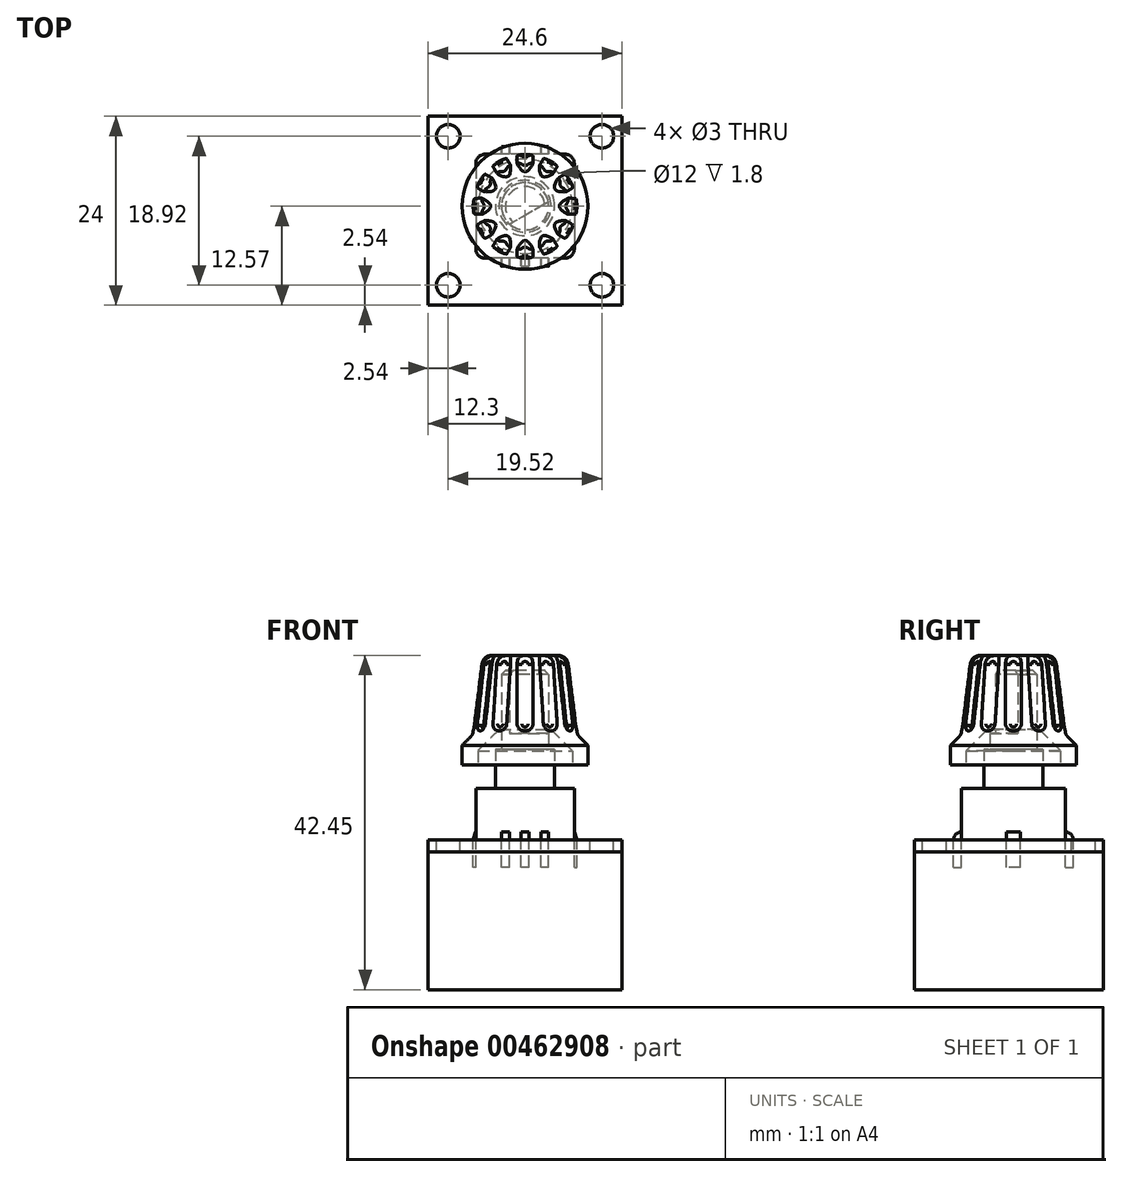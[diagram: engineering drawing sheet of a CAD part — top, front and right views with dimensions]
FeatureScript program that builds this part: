
annotation { "Feature Type Name" : "Feature", "Feature Type Description" : "" }
export const myFeature = defineFeature(function(context is Context, id is Id, definition is map)
    precondition{}
    {
        {
            var Q0;
            Q0=qCreatedBy(makeId("Top.planeOp"),FACE);
            var sketch = newSketch(context, id + "F0", { "sketchPlane" : qUnion([Q0])});
            skLineSegment(sketch, "E0.bottom", {"start": v(6.25, 6.6) * mm, "end": v(-6.25, 6.6) * mm});
            skLineSegment(sketch, "E0.top", {"start": v(6.25, -6.6) * mm, "end": v(-6.25, -6.6) * mm});
            skLineSegment(sketch, "E0.left", {"start": v(6.25, 6.6) * mm, "end": v(6.25, -6.6) * mm});
            skLineSegment(sketch, "E0.right", {"start": v(-6.25, 6.6) * mm, "end": v(-6.25, -6.6) * mm});
            skPoint(sketch, "E0.middle", {"position": v(0, 0) * mm});
            skArc(sketch, "E1", {"start": v(6.25, 5.46) * mm, "mid": v(5.92, 6.27) * mm, "end": v(5.1, 6.6) * mm});
            skArc(sketch, "E2", {"start": v(-6.25, 5.46) * mm, "mid": v(-5.92, 6.27) * mm, "end": v(-5.1, 6.6) * mm});
            skLineSegment(sketch, "E3", {"start": v(0, 0) * mm, "end": v(0, 0) * mm});
            skPoint(sketch, "E3.endSnap0", {"position": v(6.25, 0) * mm});
            skLineSegment(sketch, "E4", {"start": v(0, 0) * mm, "end": v(0, 9.01) * mm, "construction": true});
            skArc(sketch, "E5.MirrorCS", {"start": v(-6.25, -5.46) * mm, "mid": v(-5.92, -6.27) * mm, "end": v(-5.1, -6.6) * mm});
            skArc(sketch, "E6.MirrorCS", {"start": v(6.25, -5.46) * mm, "mid": v(5.92, -6.27) * mm, "end": v(5.1, -6.6) * mm});
            skCircle(sketch, "E7", {"center": v(0, 0) * mm, "radius": 3.75 * mm});
            skCircle(sketch, "E8", {"center": v(0, 0) * mm, "radius": 3 * mm});
            skLineSegment(sketch, "E9", {"start": v(6.25, 0.9) * mm, "end": v(6.6, 0.9) * mm});
            skLineSegment(sketch, "E10", {"start": v(6.6, 0.9) * mm, "end": v(6.6, -0.9) * mm});
            skLineSegment(sketch, "E11", {"start": v(6.6, -0.9) * mm, "end": v(6.25, -0.9) * mm});
            skLineSegment(sketch, "E12", {"start": v(-6.25, 0.9) * mm, "end": v(-6.6, 0.9) * mm});
            skLineSegment(sketch, "E13", {"start": v(-6.6, 0.9) * mm, "end": v(-6.6, -0.9) * mm});
            skLineSegment(sketch, "E14", {"start": v(-6.6, -0.9) * mm, "end": v(-6.25, -0.9) * mm});
            skPoint(sketch, "E15", {"position": v(6.6, 0) * mm});
            skLineSegment(sketch, "E16", {"start": v(-0.5, -6.6) * mm, "end": v(-0.5, -7.6) * mm});
            skLineSegment(sketch, "E17", {"start": v(-0.5, -7.6) * mm, "end": v(0.5, -7.6) * mm});
            skLineSegment(sketch, "E18", {"start": v(0.5, -7.6) * mm, "end": v(0.5, -6.6) * mm});
            skPoint(sketch, "E19", {"position": v(0, -7.6) * mm});
            skLineSegment(sketch, "E20", {"start": v(2, -6.6) * mm, "end": v(2, -7.6) * mm});
            skLineSegment(sketch, "E21", {"start": v(2, -7.6) * mm, "end": v(3, -7.6) * mm});
            skLineSegment(sketch, "E22", {"start": v(3, -7.6) * mm, "end": v(3, -6.6) * mm});
            skLineSegment(sketch, "E23", {"start": v(-2, -6.6) * mm, "end": v(-2, -7.6) * mm});
            skLineSegment(sketch, "E24", {"start": v(-2, -7.6) * mm, "end": v(-3, -7.6) * mm});
            skLineSegment(sketch, "E25", {"start": v(-3, -7.6) * mm, "end": v(-3, -6.6) * mm});
            skPoint(sketch, "E26", {"position": v(-2.5, -7.6) * mm});
            skPoint(sketch, "E27", {"position": v(2.5, -7.6) * mm});
            skLineSegment(sketch, "E28", {"start": v(-2, -7.6) * mm, "end": v(-0.5, -7.6) * mm, "construction": true});
            skLineSegment(sketch, "E29", {"start": v(0.5, -7.6) * mm, "end": v(2, -7.6) * mm, "construction": true});
            skLineSegment(sketch, "E30.MirrorCS", {"start": v(-3, 7.6) * mm, "end": v(-3, 6.6) * mm});
            skLineSegment(sketch, "E31.MirrorCS", {"start": v(-2, 7.6) * mm, "end": v(-3, 7.6) * mm});
            skLineSegment(sketch, "E32.MirrorCS", {"start": v(-2, 6.6) * mm, "end": v(-2, 7.6) * mm});
            skLineSegment(sketch, "E33.MirrorCS", {"start": v(2, 6.6) * mm, "end": v(2, 7.6) * mm});
            skLineSegment(sketch, "E34.MirrorCS", {"start": v(2, 7.6) * mm, "end": v(3, 7.6) * mm});
            skLineSegment(sketch, "E35.MirrorCS", {"start": v(3, 7.6) * mm, "end": v(3, 6.6) * mm});
            skLineSegment(sketch, "E36", {"start": v(2.95, 0.55) * mm, "end": v(-1.95, -2.28) * mm});
            skLineSegment(sketch, "E37", {"start": v(0, 0) * mm, "end": v(10.13, 0) * mm, "construction": true});
            skLineSegment(sketch, "E38", {"start": v(0, 0) * mm, "end": v(-2.6, -1.5) * mm, "construction": true});
            skSolve(sketch);
        }
        {
            var Q0;
            {var subQ3=sQuery(id+"F0.wireOp",EDGE,"CTmPjIdn-6teS-sF9U-aKKL-pw7HEeKchRhR");Q0=makeQuery(id+"F0.imprint","IMPRINT",FACE,{"disambiguationData":[TD([[makeQuery(id+"F0.imprint","IMPRINT",EDGE,{"derivedFrom":subQ3}),1.0]])]});}
            var Q1;
            Q1=makeQuery(id+"F0.imprint","IMPRINT",FACE,{"disambiguationData":[TD([[makeQuery(id+"F0.imprint","IMPRINT",EDGE,{"derivedFrom":sQuery(id+"F0.wireOp",EDGE,"E7")}),1.0]])]});
            var Q2;
            Q2=makeQuery(id+"F0.imprint","IMPRINT",FACE,{"disambiguationData":[TD([[makeQuery(id+"F0.imprint","IMPRINT",EDGE,{"derivedFrom":sQuery(id+"F0.wireOp",EDGE,"E8")}),1.0]])]});
            var Q3;
            {var subQ3=sQuery(id+"F0.wireOp",EDGE,"E1");Q3=makeQuery(id+"F0.imprint","IMPRINT",FACE,{"disambiguationData":[TD([[makeQuery(id+"F0.imprint","IMPRINT",EDGE,{"derivedFrom":subQ3}),1.0]])]});}
            extrude(context, id + "F1", {"entities" : qUnion([Q0, Q1, Q2, Q3]), "oppositeDirection" : true, "depth" : 6.5 * mm, "offsetDistance" : 25.4 * mm});
        }
        {
            var Q0;
            Q0=makeQuery(id+"F0.imprint","IMPRINT",FACE,{"disambiguationData":[TD([[makeQuery(id+"F0.imprint","IMPRINT",EDGE,{"derivedFrom":sQuery(id+"F0.wireOp",EDGE,"E7")}),1.0]])]});
            extrude(context, id + "F2", {"entities" : qUnion([Q0]), "operationType" : NewBodyOperationType.ADD, "depth" : 5 * mm, "offsetDistance" : 25.4 * mm});
        }
        {
            var Q0;
            {var subQ0=sQuery(id+"F0.wireOp",EDGE,"E36");Q0=makeQuery(id+"F0.imprint","IMPRINT",FACE,{"disambiguationData":[TD([[makeQuery(id+"F0.imprint","IMPRINT",EDGE,{"derivedFrom":subQ0}),-1.0]])]});}
            extrude(context, id + "F3", {"entities" : qUnion([Q0]), "depth" : 15 * mm, "offsetDistance" : 25.4 * mm});
        }
        {
            var Q0;
            {var subQ0=sQuery(id+"F0.wireOp",EDGE,"E36");Q0=makeQuery(id+"F0.imprint","IMPRINT",FACE,{"disambiguationData":[TD([[makeQuery(id+"F0.imprint","IMPRINT",EDGE,{"derivedFrom":subQ0}),1.0]])]});}
            extrude(context, id + "F4", {"entities" : qUnion([Q0]), "operationType" : NewBodyOperationType.ADD, "depth" : 13 * mm - 6 * mm, "offsetDistance" : 25.4 * mm});
        }
        {
            var Q0;
            Q0=makeQuery(id+"F3.opExtrude","CAP_EDGE",EDGE,{"disambiguationData":[OSD([sQuery(id+"F0.wireOp",EDGE,"E8")])],"isStart":false});
            chamfer(context, id + "F5", {"entities" : qUnion([Q0]), "width" : .5 * mm, "tangentPropagation" : true});
        }
        {
            var Q0;
            {var subQ0=sQuery(id+"F0.wireOp",EDGE,"E12");Q0=makeQuery(id+"F0.imprint","IMPRINT",FACE,{"disambiguationData":[TD([[makeQuery(id+"F0.imprint","IMPRINT",EDGE,{"derivedFrom":subQ0}),1.0]])]});}
            var Q1;
            {var subQ0=sQuery(id+"F0.wireOp",EDGE,"E9");Q1=makeQuery(id+"F0.imprint","IMPRINT",FACE,{"disambiguationData":[TD([[makeQuery(id+"F0.imprint","IMPRINT",EDGE,{"derivedFrom":subQ0}),-1.0]])]});}
            extrude(context, id + "F6", {"entities" : qUnion([Q0, Q1]), "operationType" : NewBodyOperationType.ADD, "oppositeDirection" : true, "depth" : 10 * mm, "offsetDistance" : 25.4 * mm, "hasSecondDirection" : true, "secondDirectionOppositeDirection" : true, "secondDirectionDepth" : 5.5 * mm});
        }
        {
            var Q0;
            {var subQ0=sQuery(id+"F0.wireOp",EDGE,"E23");Q0=makeQuery(id+"F0.imprint","IMPRINT",FACE,{"disambiguationData":[TD([[makeQuery(id+"F0.imprint","IMPRINT",EDGE,{"derivedFrom":subQ0}),-1.0]])]});}
            var Q1;
            {var subQ0=sQuery(id+"F0.wireOp",EDGE,"E16");Q1=makeQuery(id+"F0.imprint","IMPRINT",FACE,{"disambiguationData":[TD([[makeQuery(id+"F0.imprint","IMPRINT",EDGE,{"derivedFrom":subQ0}),1.0]])]});}
            var Q2;
            {var subQ0=sQuery(id+"F0.wireOp",EDGE,"E20");Q2=makeQuery(id+"F0.imprint","IMPRINT",FACE,{"disambiguationData":[TD([[makeQuery(id+"F0.imprint","IMPRINT",EDGE,{"derivedFrom":subQ0}),1.0]])]});}
            var Q3;
            {var subQ0=sQuery(id+"F0.wireOp",EDGE,"E30.MirrorCS");Q3=makeQuery(id+"F0.imprint","IMPRINT",FACE,{"disambiguationData":[TD([[makeQuery(id+"F0.imprint","IMPRINT",EDGE,{"derivedFrom":subQ0}),1.0]])]});}
            var Q4;
            {var subQ0=sQuery(id+"F0.wireOp",EDGE,"E33.MirrorCS");Q4=makeQuery(id+"F0.imprint","IMPRINT",FACE,{"disambiguationData":[TD([[makeQuery(id+"F0.imprint","IMPRINT",EDGE,{"derivedFrom":subQ0}),-1.0]])]});}
            extrude(context, id + "F7", {"entities" : qUnion([Q0, Q1, Q2, Q3, Q4]), "operationType" : NewBodyOperationType.ADD, "oppositeDirection" : true, "depth" : 10 * mm, "offsetDistance" : 25.4 * mm, "hasSecondDirection" : true, "secondDirectionOppositeDirection" : true, "secondDirectionDepth" : 5.5 * mm});
        }
        {
            var Q0;
            Q0=makeQuery(id+"F7.opExtrude","CAP_EDGE",EDGE,{"disambiguationData":[OSD([sQuery(id+"F0.wireOp",EDGE,"E24")])],"isStart":true});
            var Q1;
            Q1=makeQuery(id+"F7.opExtrude","CAP_EDGE",EDGE,{"disambiguationData":[OSD([sQuery(id+"F0.wireOp",EDGE,"E17")])],"isStart":true});
            var Q2;
            Q2=makeQuery(id+"F7.opExtrude","CAP_EDGE",EDGE,{"disambiguationData":[OSD([sQuery(id+"F0.wireOp",EDGE,"E21")])],"isStart":true});
            var Q3;
            Q3=makeQuery(id+"F7.opExtrude","CAP_EDGE",EDGE,{"disambiguationData":[OSD([sQuery(id+"F0.wireOp",EDGE,"E34.MirrorCS")])],"isStart":true});
            var Q4;
            Q4=makeQuery(id+"F7.opExtrude","CAP_EDGE",EDGE,{"disambiguationData":[OSD([sQuery(id+"F0.wireOp",EDGE,"E31.MirrorCS")])],"isStart":true});
            fillet(context, id + "F8", {"entities" : qUnion([Q0, Q1, Q2, Q3, Q4]), "radius" : 1 * mm, "tangentPropagation" : true, "allowEdgeOverflow" : false});
        }
        {
            var Q0;
            Q0=makeQuery(id+"F6.opExtrude","CAP_EDGE",EDGE,{"disambiguationData":[OSD([sQuery(id+"F0.wireOp",EDGE,"E10")])],"isStart":true});
            chamfer(context, id + "F9", {"entities" : qUnion([Q0]), "chamferType" : ChamferType.TWO_OFFSETS, "width1" : 1 * mm, "oppositeDirection" : false, "width2" : .3 * mm, "tangentPropagation" : true});
        }
        {
            var Q0;
            Q0=makeQuery(id+"F6.opExtrude","CAP_EDGE",EDGE,{"disambiguationData":[OSD([sQuery(id+"F0.wireOp",EDGE,"E13")])],"isStart":true});
            chamfer(context, id + "F10", {"entities" : qUnion([Q0]), "chamferType" : ChamferType.TWO_OFFSETS, "width1" : .3 * mm, "oppositeDirection" : false, "width2" : 1 * mm, "tangentPropagation" : true});
        }
        {
            var Q0;
            Q0=qCreatedBy(makeId("Top.planeOp"),FACE);
            cPlane(context, id + "F11", {"entities" : qUnion([Q0]), "cplaneType" : CPlaneType.OFFSET, "offset" : 3 * mm, "width" : 152.4 * mm, "height" : 152.4 * mm});
        }
        {
            var Q0;
            Q0=qCreatedBy(id+"F11.planeOp",FACE);
            var sketch = newSketch(context, id + "F12", { "sketchPlane" : qUnion([Q0])});
            skLineSegment(sketch, "E39", {"start": v(-9.63, 0) * mm, "end": v(11.95, 0) * mm, "construction": true});
            skSolve(sketch);
        }
        {
            var Q0;
            Q0=qCreatedBy(makeId("Front.planeOp"),FACE);
            var sketch = newSketch(context, id + "F13", { "sketchPlane" : qUnion([Q0])});
            skLineSegment(sketch, "E40.0", {"start": v(-9.63, 3) * mm, "end": v(11.95, 3) * mm});
            skLineSegment(sketch, "E41", {"start": v(0, -8.52) * mm, "end": v(0, 23.81) * mm, "construction": true});
            skLineSegment(sketch, "E42", {"start": v(8, 3) * mm, "end": v(8, 5.5) * mm});
            skLineSegment(sketch, "E43", {"start": v(8, 5.5) * mm, "end": v(6.65, 6.85) * mm});
            skLineSegment(sketch, "E44", {"start": v(6.65, 6.85) * mm, "end": v(5.55, 15.78) * mm});
            skLineSegment(sketch, "E45", {"start": v(4.29, 16.9) * mm, "end": v(0, 16.9) * mm});
            skPoint(sketch, "E46.visualSharp", {"position": v(5.41, 16.9) * mm});
            skArc(sketch, "E46.filletArc", {"start": v(5.55, 15.78) * mm, "mid": v(5.13, 16.58) * mm, "end": v(4.29, 16.9) * mm});
            skLineSegment(sketch, "E47", {"start": v(0, 16.9) * mm, "end": v(0, 3) * mm});
            skLineSegment(sketch, "E48", {"start": v(0, 7.5) * mm, "end": v(3.3, 7.5) * mm});
            skLineSegment(sketch, "E49", {"start": v(3.3, 7.5) * mm, "end": v(6, 4.8) * mm});
            skLineSegment(sketch, "E50", {"start": v(6, 4.8) * mm, "end": v(6, 3) * mm});
            skLineSegment(sketch, "E51", {"start": v(0, 16.9) * mm, "end": v(9.89, 18.11) * mm, "construction": true});
            skLineSegment(sketch, "E52", {"start": v(5.55, 15.78) * mm, "end": v(5.06, 19.76) * mm, "construction": true});
            skPoint(sketch, "E53", {"position": v(5.33, 17.55) * mm});
            skSolve(sketch);
        }
        {
            var Q0;
            {var subQ0=sQuery(id+"F13.wireOp",EDGE,"E42");Q0=makeQuery(id+"F13.imprint","IMPRINT",FACE,{"disambiguationData":[TD([[makeQuery(id+"F13.imprint","IMPRINT",EDGE,{"derivedFrom":subQ0}),1.0]])]});}
            var Q1;
            Q1=sQuery(id+"F13.wireOp",EDGE,"E41");
            revolve(context, id + "F14", {"entities" : qUnion([Q0]), "axis" : qUnion([Q1]), "revolveType" : RevolveType.FULL});
        }
        {
            var Q0;
            Q0=sQuery(id+"F13.wireOp",VERTEX,"E53");
            var Q1;
            Q1=sQuery(id+"F13.wireOp",EDGE,"E52");
            cPlane(context, id + "F15", {"entities" : qUnion([Q0, Q1]), "cplaneType" : CPlaneType.LINE_POINT, "offset" : 25.4 * mm, "width" : 152.4 * mm, "height" : 152.4 * mm});
        }
        {
            var Q0;
            Q0=qCreatedBy(id+"F15.planeOp",FACE);
            var sketch = newSketch(context, id + "F16", { "sketchPlane" : qUnion([Q0])});
            skCircle(sketch, "E54", {"center": v(7.86, 0) * mm, "radius": 0.75 * mm});
            skSolve(sketch);
        }
        {
            var Q0;
            Q0=makeQuery(id+"F16.imprint","IMPRINT",FACE,{"disambiguationData":[TD([[makeQuery(id+"F16.imprint","IMPRINT",EDGE,{"derivedFrom":sQuery(id+"F16.wireOp",EDGE,"E54")}),1.0]])]});
            extrude(context, id + "F17", {"entities" : qUnion([Q0]), "endBound" : BoundingType.SYMMETRIC, "depth" : 20.07 * mm, "offsetDistance" : 25.4 * mm});
        }
        {
            var Q0;
            Q0=makeQuery(id+"F17.opExtrude","CAP_FACE",FACE,{"disambiguationData":[OSD([sQuery(id+"F16.wireOp",EDGE,"E54")])],"isStart":true});
            fillet(context, id + "F18", {"entities" : qUnion([Q0]), "radius" : 0.64 * mm, "allowEdgeOverflow" : false});
        }
        {
            var Q0;
            Q0=makeQuery(id+"F17.opExtrude","SWEPT_BODY",BODY,{"disambiguationData":[OSD([sQuery(id+"F16.wireOp",EDGE,"E54")])]});
            var Q1;
            Q1=sQuery(id+"F13.wireOp",EDGE,"E41");
            circularPattern(context, id + "F19", {"operationType" : NewBodyOperationType.REMOVE, "entities" : qUnion([Q0]), "axis" : qUnion([Q1]), "angle" : 360 * degree, "instanceCount" : 12, "equalSpace" : true});
        }
        {
            var Q0;
            Q0=makeQuery(id+"F14.opRevolve","SWEPT_FACE",FACE,{"disambiguationData":[OSD([sQuery(id+"F13.wireOp",EDGE,"E44")])]});
            fillet(context, id + "F20", {"entities" : qUnion([Q0]), "radius" : 0.88 * mm, "tangentPropagation" : true, "allowEdgeOverflow" : false});
        }
        {
            var Q0;
            Q0=makeQuery(id+"F1.opExtrude","CAP_FACE",FACE,{"disambiguationData":[OSD([sQuery(id+"F0.wireOp",EDGE,"E0.bottom"),sQuery(id+"F0.wireOp",EDGE,"E0.top"),sQuery(id+"F0.wireOp",EDGE,"E0.left"),sQuery(id+"F0.wireOp",EDGE,"E0.right"),sQuery(id+"F0.wireOp",EDGE,"E1"),sQuery(id+"F0.wireOp",EDGE,"E2"),sQuery(id+"F0.wireOp",EDGE,"E5.MirrorCS"),sQuery(id+"F0.wireOp",EDGE,"E6.MirrorCS")])],"isStart":false});
            var sketch = newSketch(context, id + "F21", { "sketchPlane" : qUnion([Q0])});
            skLineSegment(sketch, "E55.bottom", {"start": v(-12.3, 12.57) * mm, "end": v(12.3, 12.57) * mm});
            skLineSegment(sketch, "E55.top", {"start": v(-12.3, -11.43) * mm, "end": v(12.3, -11.43) * mm});
            skLineSegment(sketch, "E55.left", {"start": v(-12.3, 12.57) * mm, "end": v(-12.3, -11.43) * mm});
            skLineSegment(sketch, "E55.right", {"start": v(12.3, 12.57) * mm, "end": v(12.3, -11.43) * mm});
            skPoint(sketch, "E55.middle", {"position": v(0, 0.57) * mm});
            skLineSegment(sketch, "E56", {"start": v(-12.3, 10.03) * mm, "end": v(-9.76, 10.03) * mm, "construction": true});
            skLineSegment(sketch, "E57", {"start": v(-12.3, -8.89) * mm, "end": v(-9.76, -8.89) * mm, "construction": true});
            skLineSegment(sketch, "E58", {"start": v(9.76, 12.57) * mm, "end": v(9.76, 10.03) * mm, "construction": true});
            skLineSegment(sketch, "E59", {"start": v(-9.76, 12.57) * mm, "end": v(-9.76, 10.03) * mm, "construction": true});
            skLineSegment(sketch, "E60", {"start": v(9.76, -8.89) * mm, "end": v(9.76, -11.43) * mm, "construction": true});
            skLineSegment(sketch, "E61", {"start": v(-9.76, 10.03) * mm, "end": v(-9.76, -11.43) * mm, "construction": true});
            skLineSegment(sketch, "E62", {"start": v(-9.76, -8.89) * mm, "end": v(9.76, -8.89) * mm, "construction": true});
            skLineSegment(sketch, "E63", {"start": v(9.76, 10.03) * mm, "end": v(9.76, -8.89) * mm, "construction": true});
            skLineSegment(sketch, "E64", {"start": v(9.76, -8.89) * mm, "end": v(12.3, -8.89) * mm, "construction": true});
            skLineSegment(sketch, "E65", {"start": v(-9.76, 10.03) * mm, "end": v(12.3, 10.03) * mm, "construction": true});
            skCircle(sketch, "E66", {"center": v(9.76, -8.89) * mm, "radius": 1.5 * mm});
            skCircle(sketch, "E67", {"center": v(9.76, 10.03) * mm, "radius": 1.5 * mm});
            skCircle(sketch, "E68", {"center": v(-9.76, 10.03) * mm, "radius": 1.5 * mm});
            skCircle(sketch, "E69", {"center": v(-9.76, -8.89) * mm, "radius": 1.5 * mm});
            skSolve(sketch);
        }
        {
            var Q0;
            Q0=makeQuery(id+"F21.imprint","IMPRINT",FACE,{"disambiguationData":[TD([[makeQuery(id+"F21.imprint","IMPRINT",EDGE,{"derivedFrom":sQuery(id+"F21.wireOp",EDGE,"E55.bottom")}),-1.0]])]});
            var Q1;
            {var subQ3=sQuery(id+"F0.wireOp",EDGE,"E1");Q1=makeQuery(id+"F21.imprint","IMPRINT",FACE,{"disambiguationData":[TD([[makeQuery(id+"F21.imprint","IMPRINT",EDGE,{"derivedFrom":makeQuery(id+"F1.opExtrude","CAP_EDGE",EDGE,{"disambiguationData":[OSD([subQ3])],"isStart":false})}),-1.0]])]});}
            extrude(context, id + "F22", {"entities" : qUnion([Q0, Q1]), "depth" : 1.57 * mm, "offsetDistance" : 25.4 * mm});
        }
        {
            var Q0;
            Q0=makeQuery(id+"F21.imprint","IMPRINT",FACE,{"disambiguationData":[TD([[makeQuery(id+"F21.imprint","IMPRINT",EDGE,{"derivedFrom":sQuery(id+"F21.wireOp",EDGE,"E69")}),1.0]])]});
            var Q1;
            Q1=makeQuery(id+"F21.imprint","IMPRINT",FACE,{"disambiguationData":[TD([[makeQuery(id+"F21.imprint","IMPRINT",EDGE,{"derivedFrom":sQuery(id+"F21.wireOp",EDGE,"E66")}),1.0]])]});
            var Q2;
            Q2=makeQuery(id+"F21.imprint","IMPRINT",FACE,{"disambiguationData":[TD([[makeQuery(id+"F21.imprint","IMPRINT",EDGE,{"derivedFrom":sQuery(id+"F21.wireOp",EDGE,"E67")}),1.0]])]});
            var Q3;
            Q3=makeQuery(id+"F21.imprint","IMPRINT",FACE,{"disambiguationData":[TD([[makeQuery(id+"F21.imprint","IMPRINT",EDGE,{"derivedFrom":sQuery(id+"F21.wireOp",EDGE,"E68")}),1.0]])]});
            var Q4;
            {var subQ3=sQuery(id+"F0.wireOp",EDGE,"E1");Q4=makeQuery(id+"F21.imprint","IMPRINT",FACE,{"disambiguationData":[TD([[makeQuery(id+"F21.imprint","IMPRINT",EDGE,{"derivedFrom":makeQuery(id+"F1.opExtrude","CAP_EDGE",EDGE,{"disambiguationData":[OSD([subQ3])],"isStart":false})}),-1.0]])]});}
            var Q5;
            Q5=makeQuery(id+"F21.imprint","IMPRINT",FACE,{"disambiguationData":[TD([[makeQuery(id+"F21.imprint","IMPRINT",EDGE,{"derivedFrom":sQuery(id+"F21.wireOp",EDGE,"E55.bottom")}),-1.0]])]});
            extrude(context, id + "F23", {"entities" : qUnion([Q0, Q1, Q2, Q3, Q4, Q5]), "depth" : 19.05 * mm, "offsetDistance" : 25.4 * mm});
        }
    });
